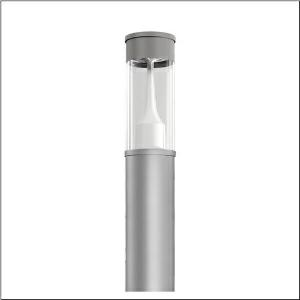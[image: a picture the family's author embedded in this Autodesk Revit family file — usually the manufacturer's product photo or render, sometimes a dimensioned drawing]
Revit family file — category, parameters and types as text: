
# Revit family: city-light_400_iq___p1_0a_5xa5305nf14hp_4342
name_source: partatom
category: Lighting Fixtures
units: mm (PartAtom-declared; Revit-internal decimal feet)

## family parameters
Cut with Voids When Loaded = No
Host = Face
Light Source = No
Part Type = Normal
Room Calculation Point = No
Round Connector Dimension = Use Diameter
Shared = No

## types (1)
- --- (1 x LED, 4210 lm, 33.6 W, 2700K)
    Apparent Load = 34 VA
    CIE Flux Codes = 31 62 91 95 100
    Color Rendering = 70
    Color Temperature = 2700K
    Default Elevation = 1800 mm
    Description = City-Light 400 iQ, light pillar, Module 540 iQ-SR, primary light control with 3 zone facetted reflector, of plastic, silver coated, highly specular, structured, primary optical cover: cover, of PMMA, transparent, partly coated, light distribution: P1.0a, primary light characteristic: strongly asymmetric, LED, High Power LED, rated luminous flux: 4.210lm, luminous efficacy: 125lm/W, light colour: 727, colour temperature: 2700K, control gear: ECG iQ, control: presetting dimming logarithmic, Street-Remote, Auto-Match, Temp-Guard, Lumen-Switch, Night-Set, Smart-Wire, Light-Fading, Desk-Remote (wireless, voltage-free reading and setting of iQ features in the workshop via application-optimized NFC function/RFID function), optimised constant luminous flux control (CLO 2.0), with terminal, 6-pole, max. 2.5mm², mains connection: 230..240V, AC, 50/60Hz, start of lifetime: 34W, end of service life: 36W, reduction: 15W, luminaire housing, cylindrical, of extruded aluminium section, coated, Siteco® metallic grey (DB 702S), length: 4.694mm, diameter: 200mm, Module 540 iQ-SR, traffic white (RAL 9016), equipment: Power, protection rating (complete): IP65, insulation class (complete): insulation class II (safety insulation), certification: CE, ENEC, VDE, packaging unit: 1 piece

Light Distribution: P1.0a
    Height = 500 mm
    Lamp = 1 x LED
    Lamp Light Flux = 4210 lm
    Lamp Power = 33.6 W
    Lamp count = 1
    Length = 200 mm  [stored 0.656168 ft]
    Luminous efficacy = 125 lm/W
    Manufacturer = Siteco
    ModVariant = No
    Model = 5XA5305NF14HP
    Mounting Place = Floor
    Mounting Type = Freestanding
    Number of Poles = 1
    OnlyDefault = Yes
    Power Factor = 1
    Product Name = City-Light 400 iQ | P1.0a
    Product group = light pillar
    ProductGroupID = 1303
    Protection Class = Protection class II
    Protection Degree = IP 65
    RLX_Detail_Level = 1
    RLX_Emergency_Light_Flux = 0 lm
    RLX_Emergency_Type = 0
    RLX_Emergency_Type_DB = No
    RlxData = <blob elided: 53597 chars, md5=73e7a531>
    Socket = socket
    Standby Power = 0 W
    System Light Flux = 4210 lm
    System Power = 34 W
    Type Comments = factory setting: luminous flux: 100 % | dim-lin: 254 | 695 mA
    Type Image = l_1006916.jpg
    URL = http://relux.com
    VarID = @adj_102621
    Voltage = 0 V
    Weight = 0.00 kg
    Width = 0 mm  [stored 0 ft]

note: [stored X ft] marks values corroborated as IEEE doubles in the binary element streams (Revit-internal decimal feet)

## geometry (parser evidence)
native form markers: Blend x4, Sweep x12
no freeform markers — native parametric forms only
